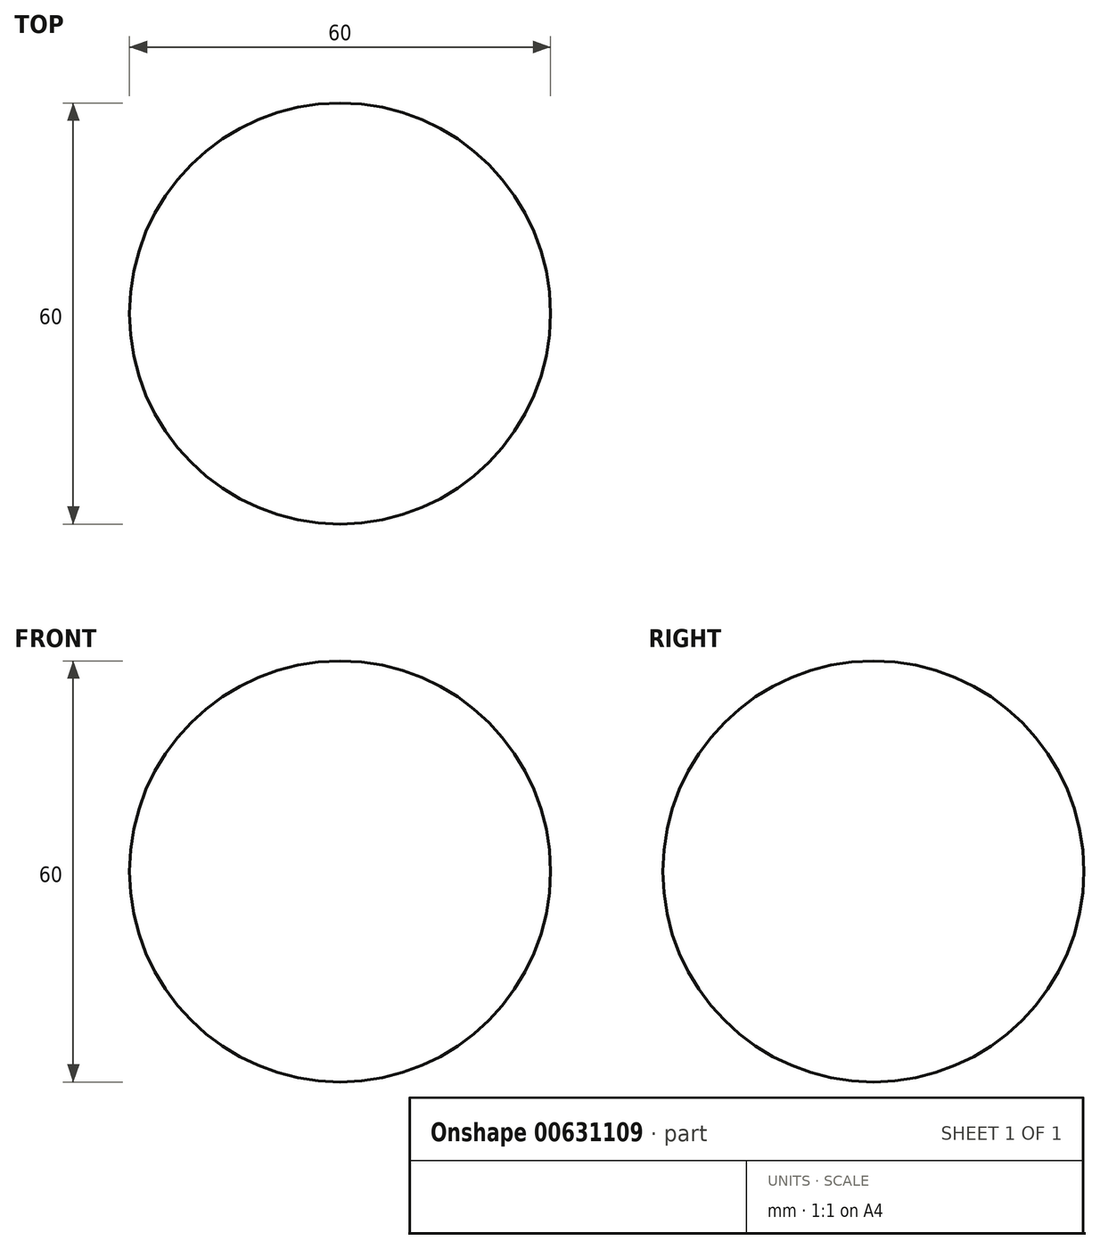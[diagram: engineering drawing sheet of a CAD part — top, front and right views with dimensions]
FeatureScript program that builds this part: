
annotation { "Feature Type Name" : "Feature", "Feature Type Description" : "" }
export const myFeature = defineFeature(function(context is Context, id is Id, definition is map)
    precondition{}
    {
        {
            var Q0;
            Q0=qCreatedBy(makeId("Front.planeOp"),FACE);
            var sketch = newSketch(context, id + "F0", { "sketchPlane" : qUnion([Q0])});
            skLineSegment(sketch, "E0", {"start": v(0, 0) * mm, "end": v(0, 60) * mm});
            skArc(sketch, "E1", {"start": v(0, 0) * mm, "mid": v(30, 30) * mm, "end": v(0, 60) * mm});
            skSolve(sketch);
        }
        {
            var Q0;
            Q0=makeQuery(id+"F0.imprint","IMPRINT",FACE,{"disambiguationData":[TD([[makeQuery(id+"F0.imprint","IMPRINT",EDGE,{"derivedFrom":sQuery(id+"F0.wireOp",EDGE,"E0")}),-1.0]])]});
            var Q1;
            Q1=sQuery(id+"F0.wireOp",EDGE,"E0");
            revolve(context, id + "F1", {"entities" : qUnion([Q0]), "axis" : qUnion([Q1]), "revolveType" : RevolveType.FULL});
        }
    });
